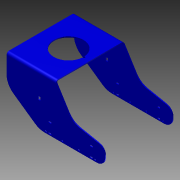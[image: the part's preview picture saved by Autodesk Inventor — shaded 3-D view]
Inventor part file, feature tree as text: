
AUTODESK INVENTOR PART (.ipt)
format: ipt  version: 2012 (Build 160160000, 160)  size: 406,016 bytes
history: native  units: mm
features: other x3, sketch x2, extrude x1
ambient origin geometry x8: Origin, YZ Plane, XZ Plane, XY Plane, X Axis, Y Axis, Z Axis, Center Point
feature tree (6):
  other  "Profile"
  extrude  "Extrusion6"  Depth=50.0mm
  other  "Bend Part11"
  other  "Bend Part12"
  sketch  "Sketch14"  dims[d1=80.0mm d2=50.0mm]
  sketch  "Sketch15"  dims[d5=200.0mm d6=100.0mm d7=70.0mm d8=180.0mm d9=20.0mm d10=100.0mm d11=50.0mm d14=50.0mm d15=25.0mm d16=5.0mm d17=5.0mm d18=150.0mm d19=5.0mm d20=5.0mm d21=30.0mm d22=10.0mm d23=6.0mm d24=97.0mm d25=73.0mm d26=4.0mm d27=8.0mm d28=8.0mm d29=7.0mm d30=4.0mm d31=8.0mm d33=8.0mm d34=1.0mm d35=8.0mm d36=4.0mm d37=7.0mm d38=8.0mm d39=4.0mm d40=8.0mm d41=30.0mm d42=8.0mm d43=1.0mm d61=30.0mm d89=8.0mm d90=4.0mm d91=8.0mm d92=4.0mm d93=30.0mm d95=7.0mm d96=5.0mm d97=8.0mm d98=4.0mm d99=8.0mm d100=4.0mm d101=30.0mm d103=7.0mm d104=5.0mm d114=90.0mm d127=97.0mm d128=6.0mm d129=10.0mm d130=73.0mm d131=65.0mm d132=100.0mm d133=200.0mm d134=5.0mm d135=2.5mm d136=50.0mm d137=2.5mm d150=5.0mm d151=5.0mm d152=50.0mm d153=5.0mm d154=5.0mm d155=50.0mm d162=5.0mm d163=5.0mm d164=50.0mm d165=5.0mm d166=5.0mm d167=50.0mm d168=3.0mm d169=0.0mm d170=5.0mm d171=90.0deg d172=5.0mm d173=90.0deg]
